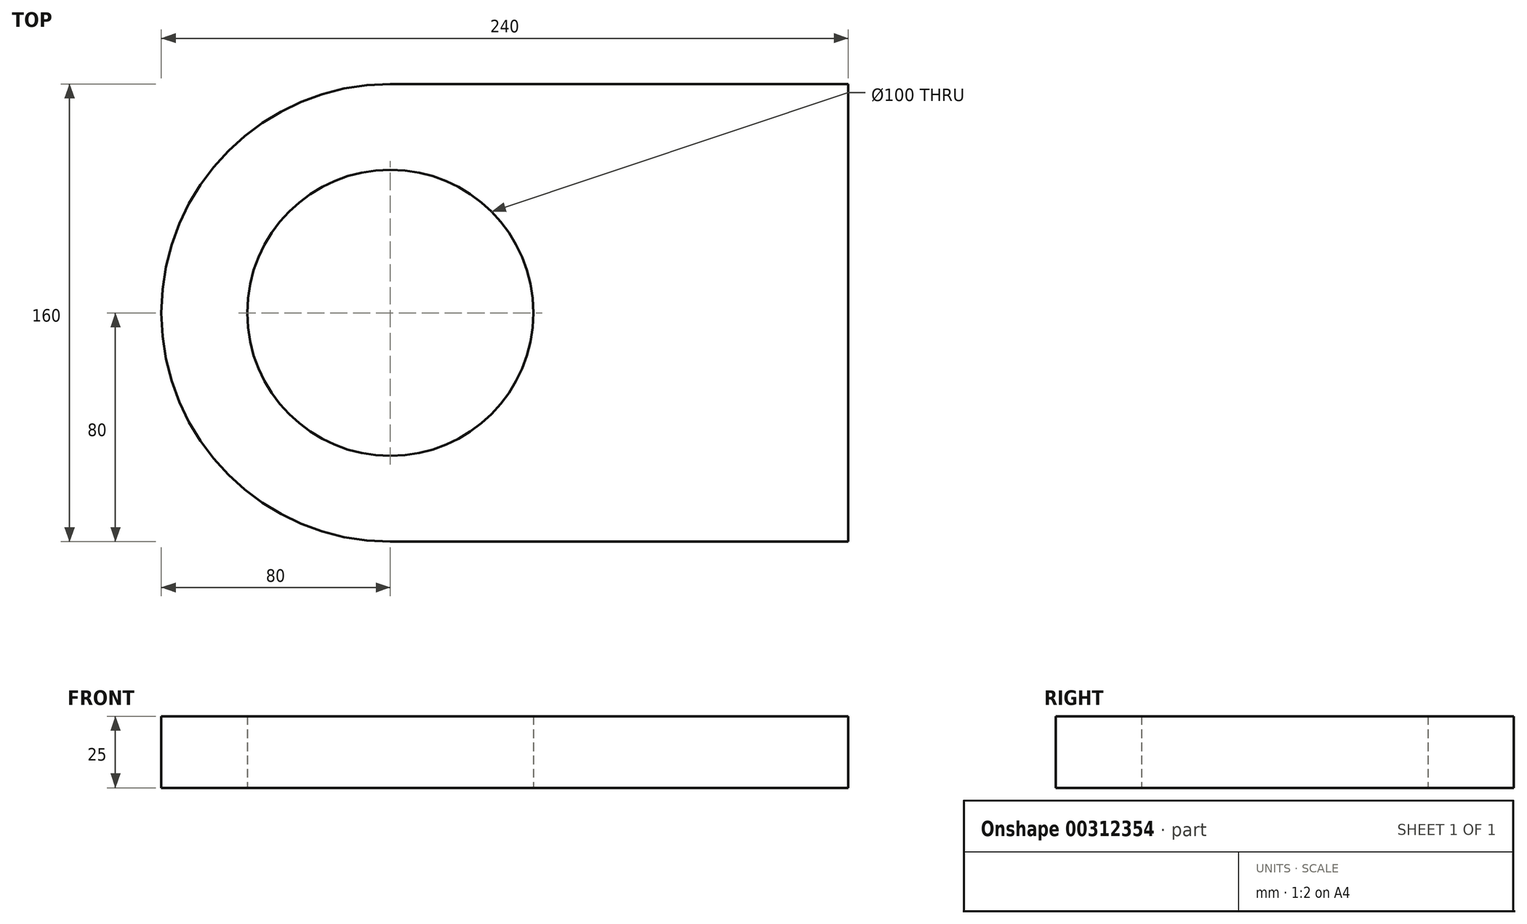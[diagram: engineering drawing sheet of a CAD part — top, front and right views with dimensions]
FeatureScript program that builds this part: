
annotation { "Feature Type Name" : "Feature", "Feature Type Description" : "" }
export const myFeature = defineFeature(function(context is Context, id is Id, definition is map)
    precondition{}
    {
        {
            var Q0;
            Q0=qCreatedBy(makeId("Top.planeOp"),FACE);
            var sketch = newSketch(context, id + "F0", { "sketchPlane" : qUnion([Q0])});
            skArc(sketch, "E0", {"start": v(0, 80) * mm, "mid": v(-80, 0) * mm, "end": v(0, -80) * mm});
            skLineSegment(sketch, "E1", {"start": v(0, 80) * mm, "end": v(160, 80) * mm});
            skLineSegment(sketch, "E2", {"start": v(0, -80) * mm, "end": v(160, -80) * mm});
            skLineSegment(sketch, "E3", {"start": v(160, -80) * mm, "end": v(160, 80) * mm});
            skCircle(sketch, "E4", {"center": v(0, 0) * mm, "radius": 50 * mm});
            skSolve(sketch);
        }
        {
            var Q0;
            Q0 = qSketchRegion(id + "F0", true);
            extrude(context, id + "F1", {"entities" : qUnion([Q0]), "depth" : 25 * mm});
        }
    });
